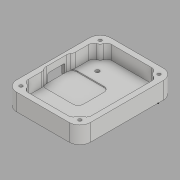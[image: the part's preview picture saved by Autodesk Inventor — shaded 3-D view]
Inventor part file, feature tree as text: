
AUTODESK INVENTOR PART (.ipt)
format: ipt  version: 2019 (Build 230136000, 136)  size: 281,088 bytes
history: native  units: in
note: dims shown in document units (in); Inventor stores cm internally (conversion verified against a paired STEP export)
features: sketch x7, extrude x4, fillet x3, hole x2
ambient origin geometry x8: Origin, YZ Plane, XZ Plane, XY Plane, X Axis, Y Axis, Z Axis, Center Point
bodies: Solid1 (feature_tree)
feature tree (16):
  extrude  "Extrusion1"  Depth=2.7224in
  sketch  "Sketch2"  dims[d2=0.1181in d3=0.0in d4=0.1969in d5=0.1969in d6=0.1969in]
  extrude  "Extrusion3"  Depth=0.1969in
  fillet  "Fillet1"  Radius=0.1969in
  fillet  "Fillet2"  Radius=0.1969in
  sketch  "Sketch4"  dims[d7=0.1969in d8=0.2362in]
  extrude  "Extrusion4"  Depth=0.2362in
  extrude  "Extrusion5"  Depth=0.2362in
  fillet  "Fillet3"  Radius=0.2362in
  hole  "Hole1"  [1 undecoded]
  hole  "Hole2"  [1 undecoded]
  sketch  "Sketch1"  dims[d0=3.4724in d1=2.7224in]
  sketch  "Sketch5"  dims[d9=0.2362in d10=0.2362in d11=0.2362in]
  sketch  "Sketch7"  dims[d12=0.2362in d13=0.2362in]
  sketch  "Sketch8"  dims[d14=0.2362in d15=0.2362in]
  sketch  "Sketch9"  dims[d16=0.188in d17=0.188in d18=0.188in d19=0.188in d20=0.188in d21=0.188in d22=0.188in d23=0.188in d24=0.188in d25=0.188in d26=0.188in d27=0.188in d28=0.188in d29=0.188in d30=0.188in d31=0.188in d32=0.188in d33=0.188in d34=0.188in d35=0.188in d36=0.188in d37=0.188in d38=0.188in d39=0.188in d42=0.5118in d43=0.0in d44=0.188in d45=0.3937in d48=0.3937in d49=0.6378in d50=0.05in d51=0.05in d52=0.05in d53=0.05in d54=0.065in d55=0.065in d56=0.1181in d57=0.0in d58=3.4724in d59=1.4173in d60=1.4173in d61=1.1654in d62=3.4724in d63=1.1417in d64=0.0787in d65=1.378in d66=0.2in d67=0.2in d68=0.2in d69=0.2in d70=0.2in d71=0.2in d72=0.2in d73=0.2in d74=0.188in d75=0.188in d76=0.188in d77=0.188in d78=1.1417in d79=0.5512in d80=0.0in d81=0.188in d82=0.188in d83=0.2756in d84=0.2756in d85=0.2756in d86=0.2756in d87=0.2756in d88=0.2756in d89=0.2756in d90=0.2756in d91=0.1181in d92=0.75in d93=0.375in d94=0.25in d95=0.5635in d96=0.3937in d97=0.0in d98=0.8in d99=0.7in d100=0.1476in d101=0.75in d102=0.375in d103=0.25in d104=0.5635in d105=0.3937in d106=0.0in d107=0.7417in]
note: 2 required parameter values undecoded (feature->parameter linkage not recoverable at this tier; creation-order binding heuristic only, values carry confidence <= 0.55)
